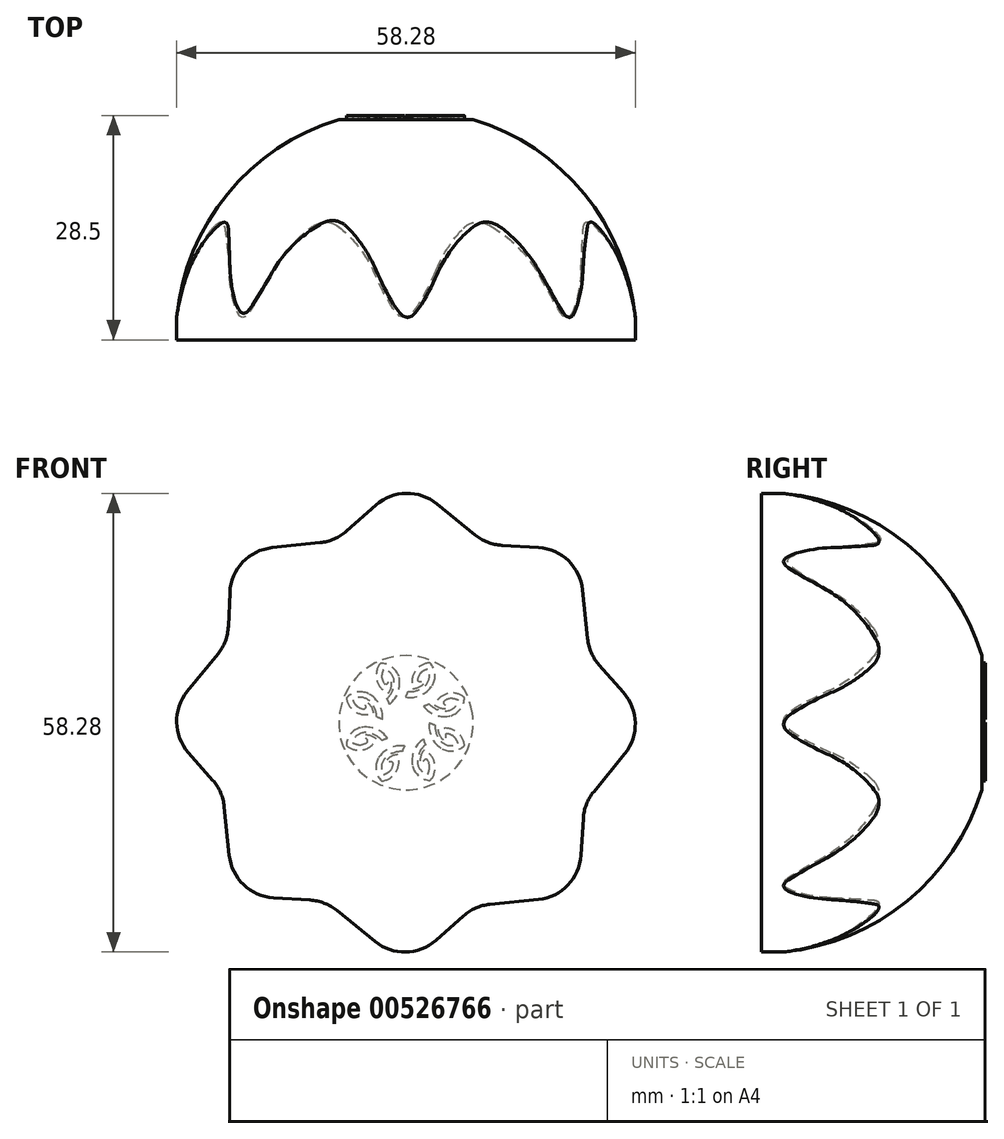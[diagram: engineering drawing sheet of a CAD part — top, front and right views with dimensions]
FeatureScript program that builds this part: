
annotation { "Feature Type Name" : "Feature", "Feature Type Description" : "" }
export const myFeature = defineFeature(function(context is Context, id is Id, definition is map)
    precondition{}
    {
        {
            var Q0;
            Q0=qCreatedBy(makeId("Front.planeOp"),FACE);
            var sketch = newSketch(context, id + "F0", { "sketchPlane" : qUnion([Q0])});
            skLineSegment(sketch, "E0", {"start": v(-3.81, 27.63) * mm, "end": v(-7.55, 24.33) * mm});
            skLineSegment(sketch, "E1", {"start": v(-10.91, 22.86) * mm, "end": v(-16.98, 22.24) * mm});
            skLineSegment(sketch, "E2", {"start": v(-22.56, 12.24) * mm, "end": v(-22.36, 16.54) * mm});
            skLineSegment(sketch, "E3", {"start": v(-23.9, 8.73) * mm, "end": v(-27.79, 3.95) * mm});
            skLineSegment(sketch, "E4", {"start": v(-24.54, -7.31) * mm, "end": v(-27.63, -3.81) * mm});
            skLineSegment(sketch, "E5", {"start": v(-23.07, -10.67) * mm, "end": v(-22.44, -16.86) * mm});
            skLineSegment(sketch, "E6", {"start": v(-16.84, -22.24) * mm, "end": v(-12.18, -22.53) * mm});
            skLineSegment(sketch, "E7", {"start": v(-8.77, -23.86) * mm, "end": v(-3.95, -27.79) * mm});
            skLineSegment(sketch, "E8", {"start": v(3.81, -27.63) * mm, "end": v(7.31, -24.54) * mm});
            skLineSegment(sketch, "E9", {"start": v(10.67, -23.07) * mm, "end": v(16.86, -22.44) * mm});
            skLineSegment(sketch, "E10", {"start": v(22.24, -16.84) * mm, "end": v(22.53, -12.18) * mm});
            skLineSegment(sketch, "E11", {"start": v(23.86, -8.77) * mm, "end": v(27.79, -3.95) * mm});
            skLineSegment(sketch, "E12", {"start": v(27.63, 3.81) * mm, "end": v(24.54, 7.31) * mm});
            skLineSegment(sketch, "E13", {"start": v(23.07, 10.67) * mm, "end": v(22.44, 16.86) * mm});
            skLineSegment(sketch, "E14", {"start": v(16.84, 22.24) * mm, "end": v(12.18, 22.53) * mm});
            skLineSegment(sketch, "E15", {"start": v(8.77, 23.86) * mm, "end": v(3.95, 27.79) * mm});
            skPoint(sketch, "E16.visualSharp", {"position": v(-9, 23.06) * mm});
            skArc(sketch, "E16.filletArc", {"start": v(-10.91, 22.86) * mm, "mid": v(-9.12, 23.33) * mm, "end": v(-7.55, 24.33) * mm});
            skPoint(sketch, "E17.visualSharp", {"position": v(0, 31) * mm});
            skArc(sketch, "E17.filletArc", {"start": v(3.95, 27.79) * mm, "mid": v(0.04, 29.13) * mm, "end": v(-3.81, 27.63) * mm});
            skPoint(sketch, "E18.visualSharp", {"position": v(10.26, 22.65) * mm});
            skArc(sketch, "E18.filletArc", {"start": v(8.77, 23.86) * mm, "mid": v(10.37, 22.93) * mm, "end": v(12.18, 22.53) * mm});
            skPoint(sketch, "E19.visualSharp", {"position": v(21.92, 21.92) * mm});
            skArc(sketch, "E19.filletArc", {"start": v(22.44, 16.86) * mm, "mid": v(20.63, 20.57) * mm, "end": v(16.84, 22.24) * mm});
            skPoint(sketch, "E20.visualSharp", {"position": v(23.27, 8.76) * mm});
            skArc(sketch, "E20.filletArc", {"start": v(23.07, 10.67) * mm, "mid": v(23.55, 8.88) * mm, "end": v(24.54, 7.31) * mm});
            skPoint(sketch, "E21.visualSharp", {"position": v(31, 0) * mm});
            skArc(sketch, "E21.filletArc", {"start": v(27.79, -3.95) * mm, "mid": v(29.13, -0.04) * mm, "end": v(27.63, 3.81) * mm});
            skPoint(sketch, "E22.visualSharp", {"position": v(21.92, -21.92) * mm});
            skArc(sketch, "E22.filletArc", {"start": v(16.86, -22.44) * mm, "mid": v(20.57, -20.63) * mm, "end": v(22.24, -16.84) * mm});
            skPoint(sketch, "E23.visualSharp", {"position": v(0, -31) * mm});
            skArc(sketch, "E23.filletArc", {"start": v(-3.95, -27.79) * mm, "mid": v(-0.04, -29.13) * mm, "end": v(3.81, -27.63) * mm});
            skPoint(sketch, "E24.visualSharp", {"position": v(-21.92, -21.92) * mm});
            skArc(sketch, "E24.filletArc", {"start": v(-22.44, -16.86) * mm, "mid": v(-20.63, -20.57) * mm, "end": v(-16.84, -22.24) * mm});
            skPoint(sketch, "E25.visualSharp", {"position": v(-31, 0) * mm});
            skArc(sketch, "E25.filletArc", {"start": v(-27.79, 3.95) * mm, "mid": v(-29.13, 0.04) * mm, "end": v(-27.63, -3.81) * mm});
            skPoint(sketch, "E26.visualSharp", {"position": v(-22.13, 21.71) * mm});
            skArc(sketch, "E26.filletArc", {"start": v(-16.98, 22.24) * mm, "mid": v(-20.73, 20.4) * mm, "end": v(-22.36, 16.54) * mm});
            skPoint(sketch, "E27.visualSharp", {"position": v(-23.27, -8.76) * mm});
            skArc(sketch, "E27.filletArc", {"start": v(-23.07, -10.67) * mm, "mid": v(-23.55, -8.88) * mm, "end": v(-24.54, -7.31) * mm});
            skPoint(sketch, "E28.visualSharp", {"position": v(-10.26, -22.65) * mm});
            skArc(sketch, "E28.filletArc", {"start": v(-8.77, -23.86) * mm, "mid": v(-10.37, -22.93) * mm, "end": v(-12.18, -22.53) * mm});
            skPoint(sketch, "E29.visualSharp", {"position": v(8.76, -23.27) * mm});
            skArc(sketch, "E29.filletArc", {"start": v(10.67, -23.07) * mm, "mid": v(8.88, -23.55) * mm, "end": v(7.31, -24.54) * mm});
            skPoint(sketch, "E30.visualSharp", {"position": v(22.65, -10.26) * mm});
            skArc(sketch, "E30.filletArc", {"start": v(23.86, -8.77) * mm, "mid": v(22.93, -10.37) * mm, "end": v(22.53, -12.18) * mm});
            skPoint(sketch, "E31.visualSharp", {"position": v(-22.65, 10.26) * mm});
            skArc(sketch, "E31.filletArc", {"start": v(-23.9, 8.73) * mm, "mid": v(-22.94, 10.38) * mm, "end": v(-22.56, 12.24) * mm});
            skSolve(sketch);
        }
        {
            var Q0;
            Q0=qCreatedBy(makeId("Top.planeOp"),FACE);
            var sketch = newSketch(context, id + "F1", { "sketchPlane" : qUnion([Q0])});
            skArc(sketch, "E32", {"start": v(29.27, 0) * mm, "mid": v(20.7, 20.7) * mm, "end": v(0, 29.27) * mm});
            skLineSegment(sketch, "E33", {"start": v(0, 0) * mm, "end": v(0, 29.27) * mm});
            skLineSegment(sketch, "E34", {"start": v(0, 0) * mm, "end": v(29.27, 0) * mm});
            skSolve(sketch);
        }
        {
            var Q0;
            Q0=qSketchRegion(id+"F1",true);
            var Q1;
            Q1=sQuery(id+"F1.wireOp",EDGE,"E33");
            revolve(context, id + "F2", {"entities" : qUnion([Q0]), "axis" : qUnion([Q1]), "revolveType" : RevolveType.FULL});
        }
        {
            var Q0;
            Q0=qSketchRegion(id+"F0",true);
            extrude(context, id + "F3", {"entities" : qUnion([Q0]), "operationType" : NewBodyOperationType.INTERSECT, "oppositeDirection" : true, "depth" : 28 * mm, "offsetDistance" : 25 * mm});
        }
        {
            var Q0;
            Q0=qCreatedBy(makeId("Front.planeOp"),FACE);
            var sketch = newSketch(context, id + "F4", { "sketchPlane" : qUnion([Q0])});
            skArc(sketch, "E35", {"start": v(-7.57, -2.88) * mm, "mid": v(-5.45, -3.45) * mm, "end": v(-3.73, -2.1) * mm});
            skArc(sketch, "E36", {"start": v(-5.76, -0.64) * mm, "mid": v(-7.04, -1.46) * mm, "end": v(-7.57, -2.88) * mm});
            skArc(sketch, "E37", {"start": v(-2.32, -2.01) * mm, "mid": v(-3.83, -0.8) * mm, "end": v(-5.76, -0.64) * mm});
            skArc(sketch, "E38", {"start": v(-2.32, -2.01) * mm, "mid": v(-2.69, -2.12) * mm, "end": v(-3.04, -2.27) * mm});
            skArc(sketch, "E39", {"start": v(-3.04, -2.27) * mm, "mid": v(-4, -1.53) * mm, "end": v(-5.19, -1.26) * mm});
            skArc(sketch, "E40", {"start": v(-5.19, -1.26) * mm, "mid": v(-6.21, -1.62) * mm, "end": v(-6.79, -2.54) * mm});
            skArc(sketch, "E41", {"start": v(-6.79, -2.54) * mm, "mid": v(-6.27, -2.75) * mm, "end": v(-5.72, -2.8) * mm});
            skArc(sketch, "E42", {"start": v(-3.73, -2.1) * mm, "mid": v(-4.7, -1.61) * mm, "end": v(-5.77, -1.68) * mm});
            skFitSpline(sketch, "E43", {"points": [v(-5.72, -2.8) * mm, v(-5.35, -2.7) * mm, v(-5, -2.54) * mm, v(-4.88, -2.36) * mm, v(-4.95, -2.14) * mm, v(-5.17, -1.96) * mm, v(-5.42, -1.82) * mm, v(-5.77, -1.68) * mm], "startDerivative": vector(3.62, 0.64) * mm, "endDerivative": vector(-2.32, 0.9) * mm});
            skArc(sketch, "E44", {"start": v(-3.11, -7.41) * mm, "mid": v(-1.25, -6.25) * mm, "end": v(-1.08, -4.06) * mm});
            skArc(sketch, "E45", {"start": v(-3.53, -4.56) * mm, "mid": v(-3.8, -6.06) * mm, "end": v(-3.11, -7.41) * mm});
            skArc(sketch, "E46", {"start": v(-0.18, -2.97) * mm, "mid": v(-2.1, -3.26) * mm, "end": v(-3.53, -4.56) * mm});
            skArc(sketch, "E47", {"start": v(-0.18, -2.97) * mm, "mid": v(-0.35, -3.31) * mm, "end": v(-0.48, -3.68) * mm});
            skArc(sketch, "E48", {"start": v(-0.48, -3.68) * mm, "mid": v(-1.68, -3.88) * mm, "end": v(-2.68, -4.56) * mm});
            skArc(sketch, "E49", {"start": v(-2.68, -4.56) * mm, "mid": v(-3.11, -5.56) * mm, "end": v(-2.83, -6.6) * mm});
            skArc(sketch, "E50", {"start": v(-2.83, -6.6) * mm, "mid": v(-2.33, -6.37) * mm, "end": v(-1.9, -6) * mm});
            skArc(sketch, "E51", {"start": v(-1.08, -4.06) * mm, "mid": v(-2.09, -4.44) * mm, "end": v(-2.77, -5.27) * mm});
            skFitSpline(sketch, "E52", {"points": [v(-1.9, -6) * mm, v(-1.73, -5.66) * mm, v(-1.6, -5.29) * mm, v(-1.67, -5.08) * mm, v(-1.87, -4.98) * mm, v(-2.15, -5.02) * mm, v(-2.43, -5.11) * mm, v(-2.77, -5.27) * mm], "startDerivative": vector(2, 3.09) * mm, "endDerivative": vector(-2.24, -1.1) * mm});
            skArc(sketch, "E53", {"start": v(-7.57, 3.12) * mm, "mid": v(-6.31, 1.32) * mm, "end": v(-4.12, 1.26) * mm});
            skArc(sketch, "E54", {"start": v(-4.74, 3.68) * mm, "mid": v(-6.25, 3.87) * mm, "end": v(-7.57, 3.12) * mm});
            skArc(sketch, "E55", {"start": v(-2.98, 0.41) * mm, "mid": v(-3.37, 2.3) * mm, "end": v(-4.74, 3.68) * mm});
            skArc(sketch, "E56", {"start": v(-2.98, 0.41) * mm, "mid": v(-3.34, 0.56) * mm, "end": v(-3.7, 0.67) * mm});
            skArc(sketch, "E57", {"start": v(-3.7, 0.67) * mm, "mid": v(-3.96, 1.86) * mm, "end": v(-4.7, 2.83) * mm});
            skArc(sketch, "E58", {"start": v(-4.7, 2.83) * mm, "mid": v(-5.71, 3.21) * mm, "end": v(-6.75, 2.88) * mm});
            skArc(sketch, "E59", {"start": v(-6.75, 2.88) * mm, "mid": v(-6.49, 2.39) * mm, "end": v(-6.1, 1.99) * mm});
            skArc(sketch, "E60", {"start": v(-4.12, 1.26) * mm, "mid": v(-4.55, 2.24) * mm, "end": v(-5.41, 2.88) * mm});
            skFitSpline(sketch, "E61", {"points": [v(-6.1, 1.99) * mm, v(-5.75, 1.83) * mm, v(-5.37, 1.72) * mm, v(-5.17, 1.8) * mm, v(-5.08, 2) * mm, v(-5.13, 2.28) * mm, v(-5.24, 2.55) * mm, v(-5.41, 2.88) * mm], "startDerivative": vector(3.18, -1.84) * mm, "endDerivative": vector(-1.2, 2.19) * mm});
            skArc(sketch, "E62", {"start": v(7.42, 3.2) * mm, "mid": v(5.28, 3.69) * mm, "end": v(3.61, 2.26) * mm});
            skArc(sketch, "E63", {"start": v(5.7, 0.89) * mm, "mid": v(6.95, 1.76) * mm, "end": v(7.42, 3.2) * mm});
            skArc(sketch, "E64", {"start": v(2.2, 2.12) * mm, "mid": v(3.77, 0.98) * mm, "end": v(5.7, 0.89) * mm});
            skArc(sketch, "E65", {"start": v(2.2, 2.12) * mm, "mid": v(2.57, 2.25) * mm, "end": v(2.92, 2.41) * mm});
            skArc(sketch, "E66", {"start": v(2.92, 2.41) * mm, "mid": v(3.9, 1.7) * mm, "end": v(5.1, 1.49) * mm});
            skArc(sketch, "E67", {"start": v(5.1, 1.49) * mm, "mid": v(6.11, 1.89) * mm, "end": v(6.65, 2.83) * mm});
            skArc(sketch, "E68", {"start": v(6.65, 2.83) * mm, "mid": v(6.13, 3.02) * mm, "end": v(5.57, 3.05) * mm});
            skArc(sketch, "E69", {"start": v(3.61, 2.26) * mm, "mid": v(4.6, 1.82) * mm, "end": v(5.67, 1.93) * mm});
            skFitSpline(sketch, "E70", {"points": [v(5.57, 3.05) * mm, v(5.2, 2.94) * mm, v(4.85, 2.76) * mm, v(4.75, 2.57) * mm, v(4.83, 2.36) * mm, v(5.05, 2.19) * mm, v(5.31, 2.06) * mm, v(5.67, 1.93) * mm], "startDerivative": vector(-3.6, -0.78) * mm, "endDerivative": vector(2.36, -0.8) * mm});
            skArc(sketch, "E71", {"start": v(3.05, 7.6) * mm, "mid": v(1.14, 6.5) * mm, "end": v(0.9, 4.31) * mm});
            skArc(sketch, "E72", {"start": v(3.36, 4.72) * mm, "mid": v(3.68, 6.2) * mm, "end": v(3.05, 7.6) * mm});
            skArc(sketch, "E73", {"start": v(-0.05, 3.26) * mm, "mid": v(1.87, 3.48) * mm, "end": v(3.36, 4.72) * mm});
            skArc(sketch, "E74", {"start": v(-0.05, 3.26) * mm, "mid": v(0.13, 3.6) * mm, "end": v(0.28, 3.96) * mm});
            skArc(sketch, "E75", {"start": v(0.28, 3.96) * mm, "mid": v(1.48, 4.11) * mm, "end": v(2.5, 4.76) * mm});
            skArc(sketch, "E76", {"start": v(2.5, 4.76) * mm, "mid": v(2.98, 5.74) * mm, "end": v(2.73, 6.8) * mm});
            skArc(sketch, "E77", {"start": v(2.73, 6.8) * mm, "mid": v(2.22, 6.58) * mm, "end": v(1.8, 6.23) * mm});
            skArc(sketch, "E78", {"start": v(0.9, 4.31) * mm, "mid": v(1.91, 4.66) * mm, "end": v(2.63, 5.47) * mm});
            skFitSpline(sketch, "E79", {"points": [v(1.8, 6.23) * mm, v(1.6, 5.9) * mm, v(1.46, 5.52) * mm, v(1.52, 5.32) * mm, v(1.72, 5.21) * mm, v(2, 5.24) * mm, v(2.27, 5.32) * mm, v(2.63, 5.47) * mm], "startDerivative": vector(-2.11, -3) * mm, "endDerivative": vector(2.28, 1) * mm});
            skArc(sketch, "E80", {"start": v(-3.23, 7.55) * mm, "mid": v(-3.7, 5.4) * mm, "end": v(-2.25, 3.75) * mm});
            skArc(sketch, "E81", {"start": v(-0.9, 5.85) * mm, "mid": v(-1.78, 7.09) * mm, "end": v(-3.23, 7.55) * mm});
            skArc(sketch, "E82", {"start": v(-2.1, 2.34) * mm, "mid": v(-0.97, 3.92) * mm, "end": v(-0.9, 5.85) * mm});
            skArc(sketch, "E83", {"start": v(-2.1, 2.34) * mm, "mid": v(-2.23, 2.7) * mm, "end": v(-2.4, 3.05) * mm});
            skArc(sketch, "E84", {"start": v(-2.4, 3.05) * mm, "mid": v(-1.7, 4.05) * mm, "end": v(-1.5, 5.25) * mm});
            skArc(sketch, "E85", {"start": v(-1.5, 5.25) * mm, "mid": v(-1.9, 6.25) * mm, "end": v(-2.85, 6.78) * mm});
            skArc(sketch, "E86", {"start": v(-2.85, 6.78) * mm, "mid": v(-3.04, 6.25) * mm, "end": v(-3.06, 5.7) * mm});
            skArc(sketch, "E87", {"start": v(-2.25, 3.75) * mm, "mid": v(-1.82, 4.74) * mm, "end": v(-1.94, 5.8) * mm});
            skFitSpline(sketch, "E88", {"points": [v(-3.06, 5.7) * mm, v(-2.95, 5.34) * mm, v(-2.76, 4.98) * mm, v(-2.58, 4.89) * mm, v(-2.36, 4.96) * mm, v(-2.2, 5.2) * mm, v(-2.07, 5.45) * mm, v(-1.94, 5.8) * mm], "startDerivative": vector(0.82, -3.58) * mm, "endDerivative": vector(0.79, 2.37) * mm});
            skArc(sketch, "E89", {"start": v(3.09, -7.33) * mm, "mid": v(3.66, -5.21) * mm, "end": v(2.3, -3.49) * mm});
            skArc(sketch, "E90", {"start": v(0.84, -5.52) * mm, "mid": v(1.66, -6.8) * mm, "end": v(3.09, -7.33) * mm});
            skArc(sketch, "E91", {"start": v(2.22, -2.08) * mm, "mid": v(1.01, -3.6) * mm, "end": v(0.84, -5.52) * mm});
            skArc(sketch, "E92", {"start": v(2.22, -2.08) * mm, "mid": v(2.33, -2.45) * mm, "end": v(2.48, -2.8) * mm});
            skArc(sketch, "E93", {"start": v(2.48, -2.8) * mm, "mid": v(1.74, -3.76) * mm, "end": v(1.47, -4.95) * mm});
            skArc(sketch, "E94", {"start": v(1.47, -4.95) * mm, "mid": v(1.83, -5.97) * mm, "end": v(2.75, -6.54) * mm});
            skArc(sketch, "E95", {"start": v(2.75, -6.54) * mm, "mid": v(2.95, -6.03) * mm, "end": v(3.01, -5.48) * mm});
            skArc(sketch, "E96", {"start": v(2.3, -3.49) * mm, "mid": v(1.82, -4.45) * mm, "end": v(1.88, -5.53) * mm});
            skFitSpline(sketch, "E97", {"points": [v(3.01, -5.48) * mm, v(2.91, -5.11) * mm, v(2.75, -4.75) * mm, v(2.56, -4.64) * mm, v(2.35, -4.7) * mm, v(2.17, -4.93) * mm, v(2.03, -5.18) * mm, v(1.88, -5.53) * mm], "startDerivative": vector(-0.64, 3.62) * mm, "endDerivative": vector(-0.9, -2.32) * mm});
            skArc(sketch, "E98", {"start": v(7.43, -2.91) * mm, "mid": v(6.26, -1.05) * mm, "end": v(4.07, -0.88) * mm});
            skArc(sketch, "E99", {"start": v(4.58, -3.33) * mm, "mid": v(6.07, -3.6) * mm, "end": v(7.43, -2.91) * mm});
            skArc(sketch, "E100", {"start": v(2.98, 0.02) * mm, "mid": v(3.28, -1.9) * mm, "end": v(4.58, -3.33) * mm});
            skArc(sketch, "E101", {"start": v(2.98, 0.02) * mm, "mid": v(3.33, -0.15) * mm, "end": v(3.69, -0.28) * mm});
            skArc(sketch, "E102", {"start": v(3.69, -0.28) * mm, "mid": v(3.9, -1.48) * mm, "end": v(4.58, -2.48) * mm});
            skArc(sketch, "E103", {"start": v(4.58, -2.48) * mm, "mid": v(5.58, -2.91) * mm, "end": v(6.62, -2.62) * mm});
            skArc(sketch, "E104", {"start": v(6.62, -2.62) * mm, "mid": v(6.38, -2.12) * mm, "end": v(6.02, -1.7) * mm});
            skArc(sketch, "E105", {"start": v(4.07, -0.88) * mm, "mid": v(4.46, -1.89) * mm, "end": v(5.3, -2.57) * mm});
            skFitSpline(sketch, "E106", {"points": [v(6.02, -1.7) * mm, v(5.68, -1.53) * mm, v(5.3, -1.4) * mm, v(5.1, -1.47) * mm, v(5, -1.67) * mm, v(5.04, -1.95) * mm, v(5.13, -2.23) * mm, v(5.3, -2.57) * mm], "startDerivative": vector(-3.1, 1.99) * mm, "endDerivative": vector(1.1, -2.24) * mm});
            skSolve(sketch);
        }
        {
            var Q0;
            Q0=qSketchRegion(id+"F4",true);
            extrude(context, id + "F5", {"entities" : qUnion([Q0]), "operationType" : NewBodyOperationType.ADD, "oppositeDirection" : true, "depth" : 28.5 * mm, "offsetDistance" : 25 * mm});
        }
    });
